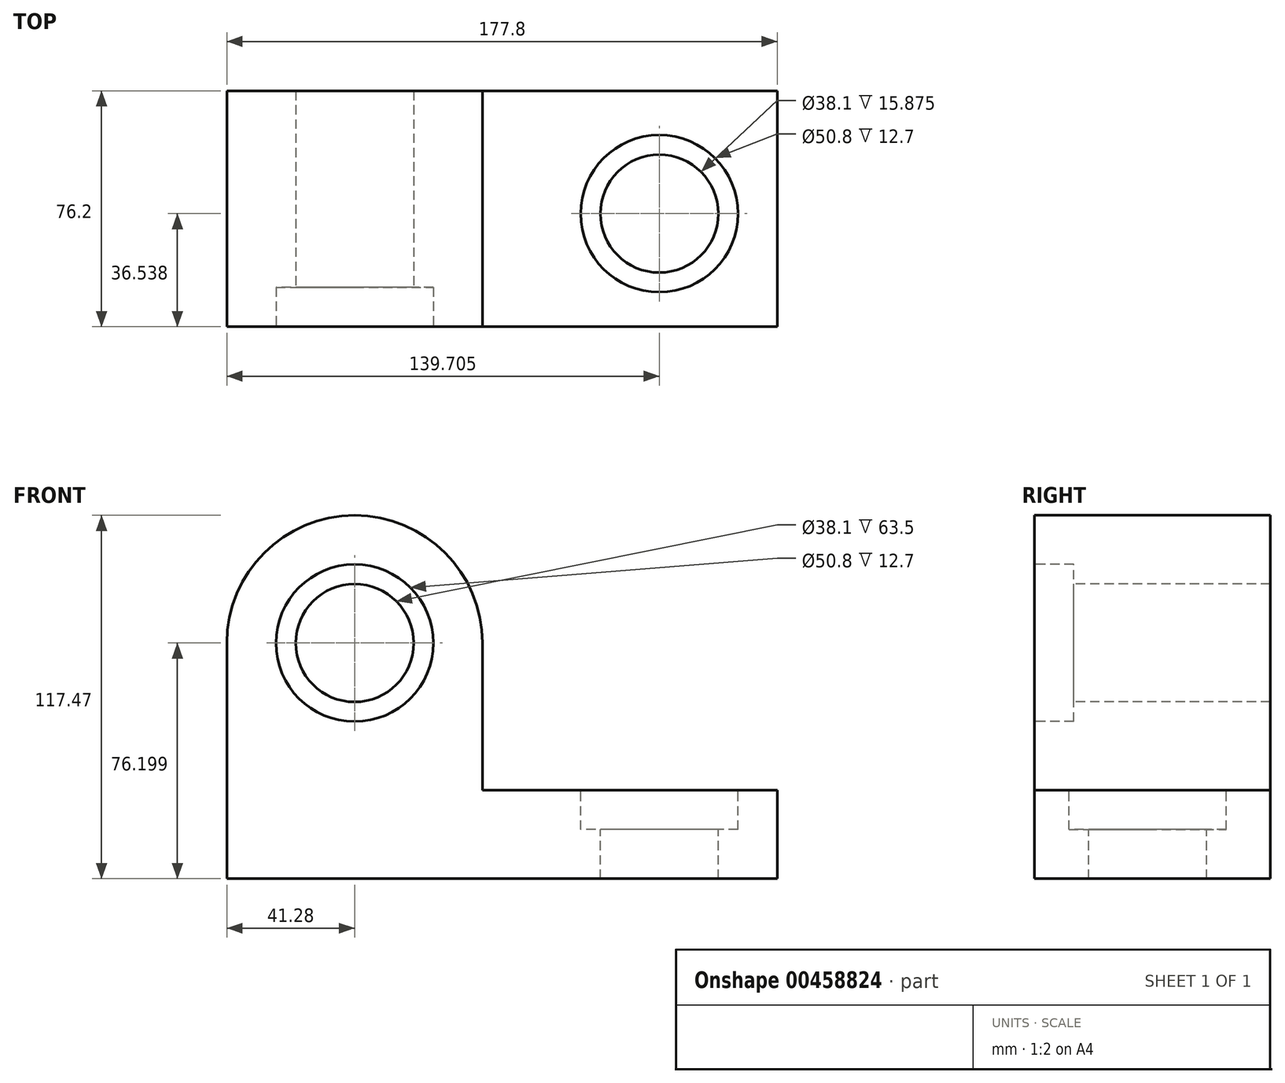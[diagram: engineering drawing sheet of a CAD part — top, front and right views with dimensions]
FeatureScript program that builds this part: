
annotation { "Feature Type Name" : "Feature", "Feature Type Description" : "" }
export const myFeature = defineFeature(function(context is Context, id is Id, definition is map)
    precondition{}
    {
        {
            var Q0;
            Q0=qCreatedBy(makeId("Front.planeOp"),FACE);
            var sketch = newSketch(context, id + "F0", { "sketchPlane" : qUnion([Q0])});
            skLineSegment(sketch, "E0.bottom", {"start": v(23.03, 20.66) * mm, "end": v(118.28, 20.66) * mm});
            skLineSegment(sketch, "E0.top", {"start": v(-59.52, -7.91) * mm, "end": v(118.28, -7.91) * mm});
            skLineSegment(sketch, "E0.left", {"start": v(-59.52, 20.66) * mm, "end": v(-59.52, -7.91) * mm});
            skLineSegment(sketch, "E0.right", {"start": v(118.28, 20.66) * mm, "end": v(118.28, -7.91) * mm});
            skLineSegment(sketch, "E1.left", {"start": v(-59.52, 20.66) * mm, "end": v(-59.52, 68.29) * mm});
            skLineSegment(sketch, "E1.right", {"start": v(23.03, 20.66) * mm, "end": v(23.03, 68.29) * mm});
            skCircle(sketch, "E2", {"center": v(-18.24, 68.29) * mm, "radius": 41.28 * mm});
            skSolve(sketch);
        }
        {
            var Q0;
            Q0=qSketchRegion(id+"F0",true);
            extrude(context, id + "F1", {"entities" : qUnion([Q0]), "depth" : 76.2 * mm});
        }
        {
            var Q0;
            Q0=makeQuery(id+"F1.opExtrude","CAP_FACE",FACE,{"disambiguationData":[OSD([sQuery(id+"F0.wireOp",EDGE,"E0.bottom"),sQuery(id+"F0.wireOp",EDGE,"E0.top"),sQuery(id+"F0.wireOp",EDGE,"E0.left"),sQuery(id+"F0.wireOp",EDGE,"E0.right"),sQuery(id+"F0.wireOp",EDGE,"E1.left"),sQuery(id+"F0.wireOp",EDGE,"E1.right"),sQuery(id+"F0.wireOp",EDGE,"E2")])],"isStart":false});
            var sketch = newSketch(context, id + "F2", { "sketchPlane" : qUnion([Q0])});
            skPoint(sketch, "E3", {"position": v(-18.24, 68.29) * mm});
            skSolve(sketch);
        }
        {
            var Q0;
            Q0=makeQuery(id+"F1.opExtrude","SWEPT_FACE",FACE,{"disambiguationData":[OSD([sQuery(id+"F0.wireOp",EDGE,"E0.bottom")])]});
            var sketch = newSketch(context, id + "F3", { "sketchPlane" : qUnion([Q0])});
            skPoint(sketch, "E4", {"position": v(80.18, -39.66) * mm});
            skSolve(sketch);
        }
        {
            var Q0;
            Q0=sQuery(id+"F2.wireOp",VERTEX,"E3");
            var Q1;
            Q1=makeQuery(id+"F1.opExtrude","SWEPT_BODY",BODY,{"disambiguationData":[OSD([sQuery(id+"F0.wireOp",EDGE,"E0.bottom"),sQuery(id+"F0.wireOp",EDGE,"E0.top"),sQuery(id+"F0.wireOp",EDGE,"E0.left"),sQuery(id+"F0.wireOp",EDGE,"E0.right"),sQuery(id+"F0.wireOp",EDGE,"E1.left"),sQuery(id+"F0.wireOp",EDGE,"E1.right"),sQuery(id+"F0.wireOp",EDGE,"E2")])]});
            hole(context, id + "F4", {"style" : HoleStyle.C_BORE, "endStyle" : HoleEndStyle.THROUGH, "holeDiameter" : 38.1 * mm, "cBoreDiameter" : 50.8 * mm, "cBoreDepth" : 12.7 * mm, "isTappedThrough" : true, "tappedDepth" : 12.7 * mm, "tapClearance" : 3, "locations" : qUnion([Q0]), "scope" : qUnion([Q1])});
        }
        {
            var Q0;
            Q0=sQuery(id+"F3.wireOp",VERTEX,"E4");
            var Q1;
            Q1=makeQuery(id+"F1.opExtrude","SWEPT_BODY",BODY,{"disambiguationData":[OSD([sQuery(id+"F0.wireOp",EDGE,"E0.bottom"),sQuery(id+"F0.wireOp",EDGE,"E0.top"),sQuery(id+"F0.wireOp",EDGE,"E0.left"),sQuery(id+"F0.wireOp",EDGE,"E0.right"),sQuery(id+"F0.wireOp",EDGE,"E1.left"),sQuery(id+"F0.wireOp",EDGE,"E1.right"),sQuery(id+"F0.wireOp",EDGE,"E2")])]});
            hole(context, id + "F5", {"style" : HoleStyle.C_BORE, "endStyle" : HoleEndStyle.THROUGH, "holeDiameter" : 38.1 * mm, "cBoreDiameter" : 50.8 * mm, "cBoreDepth" : 12.7 * mm, "isTappedThrough" : true, "tappedDepth" : 12.7 * mm, "tapClearance" : 3, "locations" : qUnion([Q0]), "scope" : qUnion([Q1])});
        }
    });
